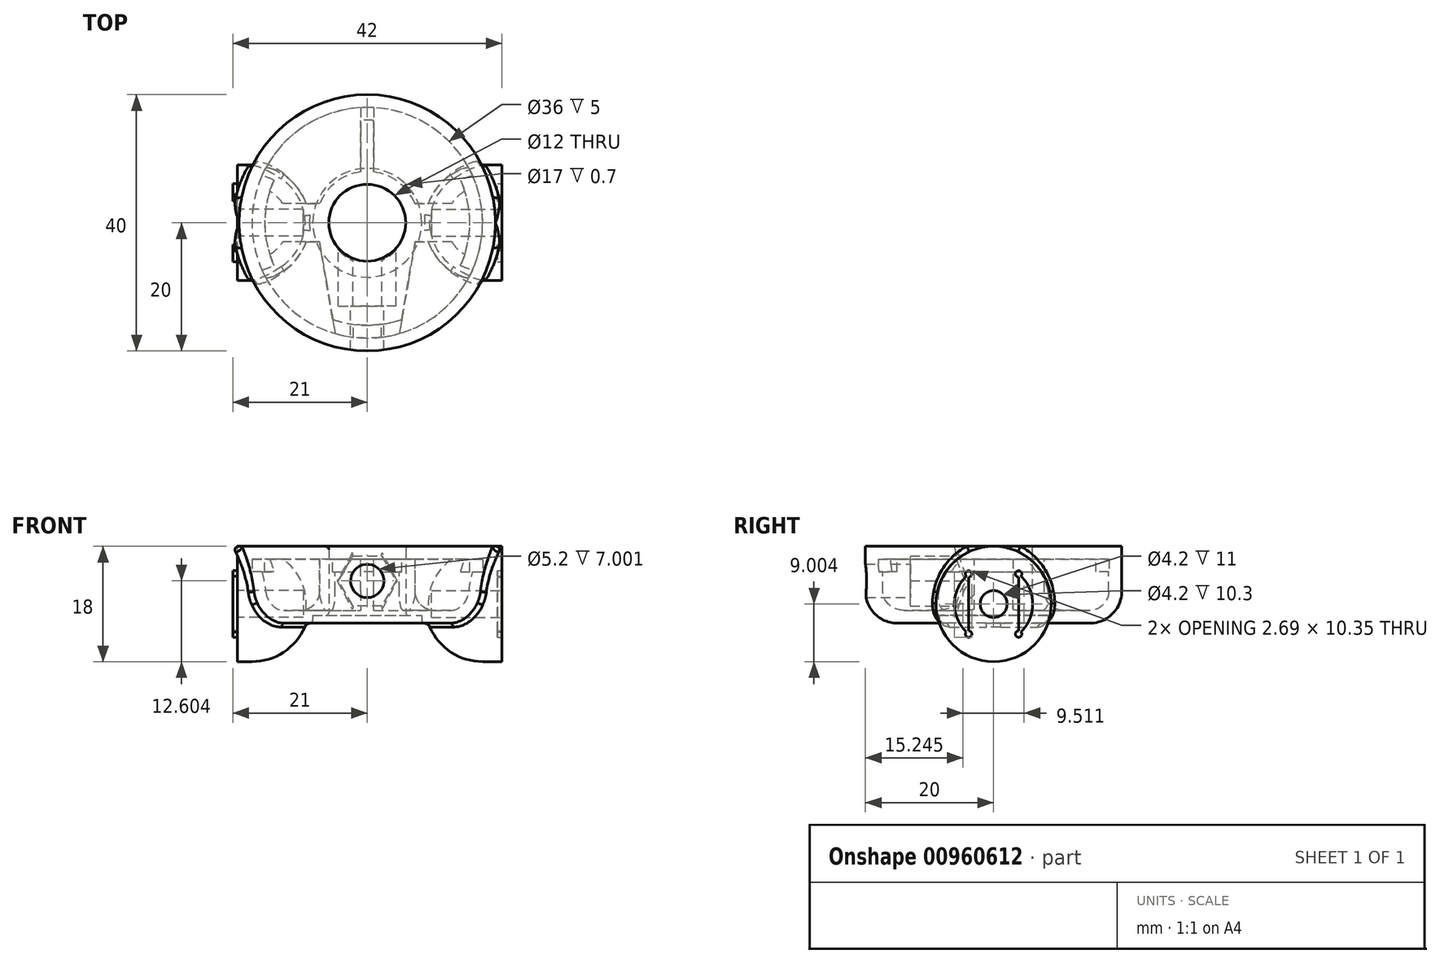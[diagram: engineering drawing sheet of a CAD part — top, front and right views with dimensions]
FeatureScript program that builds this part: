
annotation { "Feature Type Name" : "Feature", "Feature Type Description" : "" }
export const myFeature = defineFeature(function(context is Context, id is Id, definition is map)
    precondition{}
    {
        {
            var Q0;
            Q0=qCreatedBy(makeId("Front.planeOp"),FACE);
            var sketch = newSketch(context, id + "F0", { "sketchPlane" : qUnion([Q0])});
            skLineSegment(sketch, "E0", {"start": v(0, 0) * mm, "end": v(0, 29.29) * mm, "construction": true});
            skLineSegment(sketch, "E1", {"start": v(-6, 15.66) * mm, "end": v(-6, 4.86) * mm});
            skLineSegment(sketch, "E2", {"start": v(-6, 4.86) * mm, "end": v(-8.5, 4.86) * mm});
            skLineSegment(sketch, "E3", {"start": v(-8.5, 4.86) * mm, "end": v(-8.5, 3.66) * mm});
            skLineSegment(sketch, "E4", {"start": v(-8.5, 3.66) * mm, "end": v(-8.5, 3.66) * mm});
            skLineSegment(sketch, "E5", {"start": v(-8.5, 3.66) * mm, "end": v(-15, 3.66) * mm});
            skLineSegment(sketch, "E6", {"start": v(-20, 8.66) * mm, "end": v(-20, 15.66) * mm});
            skLineSegment(sketch, "E7", {"start": v(-20, 15.66) * mm, "end": v(-18, 15.66) * mm});
            skLineSegment(sketch, "E8", {"start": v(-18, 15.66) * mm, "end": v(-18, 15.66) * mm});
            skLineSegment(sketch, "E9", {"start": v(-18, 15.66) * mm, "end": v(-18, 8.66) * mm});
            skLineSegment(sketch, "E10", {"start": v(-15, 5.66) * mm, "end": v(-11, 5.66) * mm});
            skLineSegment(sketch, "E11", {"start": v(-8, 5.66) * mm, "end": v(-8, 5.66) * mm});
            skLineSegment(sketch, "E12", {"start": v(-8, 8.66) * mm, "end": v(-8, 15.66) * mm});
            skLineSegment(sketch, "E13", {"start": v(-6, 15.66) * mm, "end": v(-8, 15.66) * mm});
            skPoint(sketch, "E14.visualSharp", {"position": v(-20, 3.66) * mm});
            skArc(sketch, "E14.filletArc", {"start": v(-20, 8.66) * mm, "mid": v(-18.54, 5.13) * mm, "end": v(-15, 3.66) * mm});
            skPoint(sketch, "E15.visualSharp", {"position": v(-18, 5.66) * mm});
            skArc(sketch, "E15.filletArc", {"start": v(-18, 8.66) * mm, "mid": v(-17.12, 6.54) * mm, "end": v(-15, 5.66) * mm});
            skPoint(sketch, "E16.visualSharp", {"position": v(-8, 5.66) * mm});
            skArc(sketch, "E16.filletArc", {"start": v(-11, 5.66) * mm, "mid": v(-8.88, 6.54) * mm, "end": v(-8, 8.66) * mm});
            skSolve(sketch);
        }
        {
            var Q0;
            Q0=makeQuery(id+"F0.imprint","IMPRINT",FACE,{"disambiguationData":[TD([[makeQuery(id+"F0.imprint","IMPRINT",EDGE,{"derivedFrom":sQuery(id+"F0.wireOp",EDGE,"E1")}),-1.0]])]});
            var Q1;
            Q1=sQuery(id+"F0.wireOp",EDGE,"E0");
            revolve(context, id + "F1", {"surfaceOperationType" : NewSurfaceOperationType.NEW, "entities" : qUnion([Q0]), "axis" : qUnion([Q1]), "revolveType" : RevolveType.FULL});
        }
        {
            var Q0;
            Q0=makeQuery(id+"F1.opRevolve","SWEPT_FACE",FACE,{"disambiguationData":[OSD([sQuery(id+"F0.wireOp",EDGE,"E7")])]});
            cPlane(context, id + "F2", {"entities" : qUnion([Q0]), "cplaneType" : CPlaneType.OFFSET, "offset" : 9 * mm, "oppositeDirection" : true, "width" : 150 * mm, "height" : 150 * mm});
        }
        {
            var Q0;
            Q0=qCreatedBy(id+"F2.planeOp",FACE);
            var sketch = newSketch(context, id + "F3", { "sketchPlane" : qUnion([Q0])});
            skLineSegment(sketch, "E17.bottom", {"start": v(-9, 0) * mm, "end": v(-21, 0) * mm});
            skLineSegment(sketch, "E17.top", {"start": v(-18, -9) * mm, "end": v(-21, -9) * mm});
            skLineSegment(sketch, "E17.left", {"start": v(-9, 0) * mm, "end": v(-9, 0) * mm});
            skLineSegment(sketch, "E17.right", {"start": v(-21, 0) * mm, "end": v(-21, -9) * mm});
            skLineSegment(sketch, "E18.bottom", {"start": v(9, 0) * mm, "end": v(21, 0) * mm});
            skLineSegment(sketch, "E18.top", {"start": v(18, -9) * mm, "end": v(21, -9) * mm});
            skLineSegment(sketch, "E18.left", {"start": v(9, 0) * mm, "end": v(9, 0) * mm});
            skLineSegment(sketch, "E18.right", {"start": v(21, 0) * mm, "end": v(21, -9) * mm});
            skPoint(sketch, "E19.visualSharp", {"position": v(-9, -9) * mm});
            skArc(sketch, "E19.filletArc", {"start": v(-18, -9) * mm, "mid": v(-11.64, -6.36) * mm, "end": v(-9, 0) * mm});
            skPoint(sketch, "E20.visualSharp", {"position": v(9, -9) * mm});
            skArc(sketch, "E20.filletArc", {"start": v(9, 0) * mm, "mid": v(11.64, -6.36) * mm, "end": v(18, -9) * mm});
            skSolve(sketch);
        }
        {
            var Q0;
            Q0=makeQuery(id+"F3.imprint","IMPRINT",FACE,{"disambiguationData":[TD([[makeQuery(id+"F3.imprint","IMPRINT",EDGE,{"derivedFrom":sQuery(id+"F3.wireOp",EDGE,"E17.bottom")}),1.0]])]});
            var Q1;
            Q1=makeQuery(id+"F3.imprint","IMPRINT",FACE,{"disambiguationData":[TD([[makeQuery(id+"F3.imprint","IMPRINT",EDGE,{"derivedFrom":sQuery(id+"F3.wireOp",EDGE,"E18.bottom")}),-1.0]])]});
            var Q2;
            Q2=sQuery(id+"F3.wireOp",EDGE,"E17.bottom");
            revolve(context, id + "F4", {"operationType" : NewBodyOperationType.ADD, "surfaceOperationType" : NewSurfaceOperationType.NEW, "entities" : qUnion([Q0, Q1]), "axis" : qUnion([Q2]), "revolveType" : RevolveType.FULL});
        }
        {
            var Q0;
            Q0=makeQuery(id+"F1.opRevolve","SWEPT_FACE",FACE,{"disambiguationData":[OSD([sQuery(id+"F0.wireOp",EDGE,"E7")])]});
            var sketch = newSketch(context, id + "F5", { "sketchPlane" : qUnion([Q0])});
            skLineSegment(sketch, "E21.bottom", {"start": v(-19.77, 3) * mm, "end": v(19.77, 3) * mm});
            skLineSegment(sketch, "E21.top", {"start": v(-19.77, -3) * mm, "end": v(19.77, -3) * mm});
            skLineSegment(sketch, "E21.left", {"start": v(-19.77, 3) * mm, "end": v(-19.77, -3) * mm});
            skLineSegment(sketch, "E21.right", {"start": v(19.77, 3) * mm, "end": v(19.77, -3) * mm});
            skLineSegment(sketch, "E22", {"start": v(-7, 3) * mm, "end": v(-7, -3) * mm});
            skLineSegment(sketch, "E23", {"start": v(7, 3) * mm, "end": v(7, -3) * mm});
            skSolve(sketch);
        }
        {
            var Q0;
            {var subQ0=sQuery(id+"F5.wireOp",EDGE,"E23");Q0=makeQuery(id+"F5.imprint","IMPRINT",FACE,{"disambiguationData":[TD([[makeQuery(id+"F5.imprint","IMPRINT",EDGE,{"derivedFrom":subQ0}),1.0]])]});}
            var Q1;
            {var subQ0=sQuery(id+"F5.wireOp",EDGE,"E22");Q1=makeQuery(id+"F5.imprint","IMPRINT",FACE,{"disambiguationData":[TD([[makeQuery(id+"F5.imprint","IMPRINT",EDGE,{"derivedFrom":subQ0}),-1.0]])]});}
            extrude(context, id + "F6", {"entities" : qUnion([Q0, Q1]), "operationType" : NewBodyOperationType.ADD, "oppositeDirection" : true, "depth" : 10 * mm, "offsetDistance" : 25 * mm});
        }
        {
            var Q0;
            Q0=makeQuery(id+"F4.opRevolve","SWEPT_FACE",FACE,{"disambiguationData":[OSD([sQuery(id+"F3.wireOp",EDGE,"E18.right")])]});
            var sketch = newSketch(context, id + "F7", { "sketchPlane" : qUnion([Q0])});
            skCircle(sketch, "E24.0", {"center": v(0, 6.66) * mm, "radius": 9 * mm});
            skCircle(sketch, "E25", {"center": v(0, 6.66) * mm, "radius": 2.1 * mm});
            skSolve(sketch);
        }
        {
            var Q0;
            Q0=makeQuery(id+"F7.imprint","IMPRINT",FACE,{"disambiguationData":[TD([[makeQuery(id+"F7.imprint","IMPRINT",EDGE,{"derivedFrom":sQuery(id+"F7.wireOp",EDGE,"E25")}),1.0]])]});
            extrude(context, id + "F8", {"entities" : qUnion([Q0]), "operationType" : NewBodyOperationType.REMOVE, "oppositeDirection" : true, "depth" : 11 * mm, "offsetDistance" : 25 * mm});
        }
        {
            var Q0;
            Q0=makeQuery(id+"F4.opRevolve","SWEPT_FACE",FACE,{"disambiguationData":[OSD([sQuery(id+"F3.wireOp",EDGE,"E17.right")])]});
            var sketch = newSketch(context, id + "F9", { "sketchPlane" : qUnion([Q0])});
            skCircle(sketch, "E26.0", {"center": v(0, 6.66) * mm, "radius": 2.1 * mm});
            skSolve(sketch);
        }
        {
            var Q0;
            Q0=makeQuery(id+"F9.imprint","IMPRINT",FACE,{"disambiguationData":[TD([[makeQuery(id+"F9.imprint","IMPRINT",EDGE,{"derivedFrom":sQuery(id+"F9.wireOp",EDGE,"E26.0")}),1.0]])]});
            extrude(context, id + "F10", {"entities" : qUnion([Q0]), "operationType" : NewBodyOperationType.REMOVE, "oppositeDirection" : true, "depth" : 11 * mm, "offsetDistance" : 25 * mm});
        }
        {
            var Q0;
            {var subQ0=sQuery(id+"F5.wireOp",EDGE,"E21.top");var subQ1=sQuery(id+"F5.wireOp",EDGE,"E21.bottom");var subQ2=sQuery(id+"F0.wireOp",EDGE,"E9");var subQ3=sQuery(id+"F0.wireOp",EDGE,"E7");Q0=makeQuery(id+"F6.boolean.opBoolean","MERGE",FACE,{"derivedFrom":[makeQuery(id+"F1.opRevolve","SWEPT_FACE",FACE,{"disambiguationData":[OSD([subQ3])]}),makeQuery(id+"F1.opRevolve","SWEPT_FACE",FACE,{"disambiguationData":[OSD([sQuery(id+"F0.wireOp",EDGE,"E13")])]}),makeQuery(id+"F6.opExtrude","CAP_FACE",FACE,{"disambiguationData":[OSD([subQ3,subQ2,subQ1,subQ0,sQuery(id+"F5.wireOp",EDGE,"E22")])],"isStart":true}),makeQuery(id+"F6.opExtrude","CAP_FACE",FACE,{"disambiguationData":[OSD([subQ3,subQ2,subQ1,subQ0,sQuery(id+"F5.wireOp",EDGE,"E23")])],"isStart":true})]});}
            var sketch = newSketch(context, id + "F11", { "sketchPlane" : qUnion([Q0])});
            skLineSegment(sketch, "E27", {"start": v(-7.5, -2.78) * mm, "end": v(-5, -17.3) * mm});
            skLineSegment(sketch, "E28", {"start": v(7.5, -2.78) * mm, "end": v(5, -17.3) * mm});
            skSolve(sketch);
        }
        {
            var Q0;
            {var subQ0=sQuery(id+"F11.wireOp",EDGE,"E27");Q0=makeQuery(id+"F11.imprint","IMPRINT",FACE,{"disambiguationData":[TD([[makeQuery(id+"F11.imprint","IMPRINT",EDGE,{"derivedFrom":subQ0}),1.0]])]});}
            extrude(context, id + "F12", {"entities" : qUnion([Q0]), "operationType" : NewBodyOperationType.ADD, "oppositeDirection" : true, "depth" : 10 * mm, "offsetDistance" : 25 * mm});
        }
        {
            var Q0;
            Q0=qCreatedBy(makeId("Front.planeOp"),FACE);
            var sketch = newSketch(context, id + "F13", { "sketchPlane" : qUnion([Q0])});
            skCircle(sketch, "E29", {"center": v(0, 10.26) * mm, "radius": 2.6 * mm});
            skSolve(sketch);
        }
        {
            var Q0;
            Q0 = qSketchRegion(id + "F13", true);
            extrude(context, id + "F14", {"entities" : qUnion([Q0]), "operationType" : NewBodyOperationType.REMOVE, "depth" : 25 * mm, "offsetDistance" : 25 * mm});
        }
        {
            var Q0;
            {var subQ0=sQuery(id+"F0.wireOp",EDGE,"E13");var subQ1=sQuery(id+"F0.wireOp",EDGE,"E9");var subQ2=sQuery(id+"F0.wireOp",EDGE,"E7");var subQ3=sQuery(id+"F5.wireOp",EDGE,"E21.top");var subQ4=sQuery(id+"F5.wireOp",EDGE,"E21.bottom");Q0=makeQuery(id+"F12.boolean.opBoolean","MERGE",FACE,{"derivedFrom":[makeQuery(id+"F6.boolean.opBoolean","MERGE",FACE,{"derivedFrom":[makeQuery(id+"F1.opRevolve","SWEPT_FACE",FACE,{"disambiguationData":[OSD([subQ2])]}),makeQuery(id+"F1.opRevolve","SWEPT_FACE",FACE,{"disambiguationData":[OSD([subQ0])]}),makeQuery(id+"F6.opExtrude","CAP_FACE",FACE,{"disambiguationData":[OSD([subQ2,subQ1,subQ4,subQ3,sQuery(id+"F5.wireOp",EDGE,"E22")])],"isStart":true}),makeQuery(id+"F6.opExtrude","CAP_FACE",FACE,{"disambiguationData":[OSD([subQ2,subQ1,subQ4,subQ3,sQuery(id+"F5.wireOp",EDGE,"E23")])],"isStart":true})]}),makeQuery(id+"F12.opExtrude","CAP_FACE",FACE,{"disambiguationData":[OSD([subQ2,subQ1,sQuery(id+"F0.wireOp",EDGE,"E12"),subQ0,sQuery(id+"F11.wireOp",EDGE,"E27"),sQuery(id+"F11.wireOp",EDGE,"E28")])],"isStart":true})]});}
            var sketch = newSketch(context, id + "F15", { "sketchPlane" : qUnion([Q0])});
            skLineSegment(sketch, "E30.bottom", {"start": v(-1, 18.3) * mm, "end": v(1, 18.3) * mm});
            skLineSegment(sketch, "E30.top", {"start": v(-1, 7.14) * mm, "end": v(1, 7.14) * mm});
            skLineSegment(sketch, "E30.left", {"start": v(-1, 18.3) * mm, "end": v(-1, 7.14) * mm});
            skLineSegment(sketch, "E30.right", {"start": v(1, 18.3) * mm, "end": v(1, 7.14) * mm});
            skSolve(sketch);
        }
        {
            var Q0;
            {var subQ0=sQuery(id+"F15.wireOp",EDGE,"E30.left");var subQ1=sQuery(id+"F5.wireOp",EDGE,"E22");var subQ2=sQuery(id+"F5.wireOp",EDGE,"E21.bottom");var subQ3=sQuery(id+"F0.wireOp",EDGE,"E9");var subQ4=sQuery(id+"F0.wireOp",EDGE,"E7");var subQ5=makeQuery(id+"F1.opRevolve","SWEPT_EDGE",EDGE,{"disambiguationData":[OSD([subQ4,subQ3])]});var subQ6=makeQuery(id+"F6.opExtrude","SWEPT_FACE",FACE,{"disambiguationData":[OSD([subQ2]),TDD([makeQuery(id+"F5.imprint","IMPRINT",EDGE,{"disambiguationData":[TD([[makeQuery(id+"F5.imprint","INTERSECT",VERTEX,{"derivedFrom":[subQ2,subQ1]}),1.0]])],"derivedFrom":subQ2})])]});var subQ15=makeQuery(id+"F6.boolean.opBoolean","SPLIT",EDGE,{"disambiguationData":[TD([subQ6])],"derivedFrom":subQ5});var subQ16=makeQuery(id+"F15.imprint","INTERSECT",VERTEX,{"derivedFrom":[subQ15,subQ0]});Q0=makeQuery(id+"F15.imprint","IMPRINT",FACE,{"disambiguationData":[TD([[makeQuery(id+"F15.imprint","IMPRINT",EDGE,{"disambiguationData":[TD([[subQ16,-1.0]])],"derivedFrom":subQ0}),1.0]])]});}
            extrude(context, id + "F16", {"entities" : qUnion([Q0]), "operationType" : NewBodyOperationType.ADD, "oppositeDirection" : true, "depth" : 10 * mm, "offsetDistance" : 25 * mm});
        }
        {
            var Q0;
            Q0=makeQuery(id+"F1.opRevolve","SWEPT_EDGE",EDGE,{"disambiguationData":[OSD([sQuery(id+"F0.wireOp",EDGE,"E1"),sQuery(id+"F0.wireOp",EDGE,"E2")])]});
            var Q1;
            Q1=makeQuery(id+"F1.opRevolve","SWEPT_EDGE",EDGE,{"disambiguationData":[OSD([sQuery(id+"F0.wireOp",EDGE,"E3"),sQuery(id+"F0.wireOp",EDGE,"E5")])]});
            var Q2;
            Q2=makeQuery(id+"F1.opRevolve","SWEPT_EDGE",EDGE,{"disambiguationData":[OSD([sQuery(id+"F0.wireOp",EDGE,"E1"),sQuery(id+"F0.wireOp",EDGE,"E13")])]});
            var Q3;
            Q3=makeQuery(id+"F28.boolean.opBoolean","INTERSECT",EDGE,{"derivedFrom":[makeQuery(id+"F1.opRevolve","SWEPT_FACE",FACE,{"disambiguationData":[OSD([sQuery(id+"F0.wireOp",EDGE,"E1")])]}),makeQuery(id+"F28.opExtrude","SWEPT_FACE",FACE,{"disambiguationData":[OSD([sQuery(id+"F27.wireOp",EDGE,"E51.5")])]})]});
            var Q4;
            Q4=makeQuery(id+"F28.boolean.opBoolean","INTERSECT",EDGE,{"derivedFrom":[makeQuery(id+"F1.opRevolve","SWEPT_FACE",FACE,{"disambiguationData":[OSD([sQuery(id+"F0.wireOp",EDGE,"E1")])]}),makeQuery(id+"F28.opExtrude","SWEPT_FACE",FACE,{"disambiguationData":[OSD([sQuery(id+"F27.wireOp",EDGE,"E51.4")])]})]});
            var Q5;
            Q5=makeQuery(id+"F28.boolean.opBoolean","INTERSECT",EDGE,{"derivedFrom":[makeQuery(id+"F1.opRevolve","SWEPT_FACE",FACE,{"disambiguationData":[OSD([sQuery(id+"F0.wireOp",EDGE,"E1")])]}),makeQuery(id+"F28.opExtrude","SWEPT_FACE",FACE,{"disambiguationData":[OSD([sQuery(id+"F27.wireOp",EDGE,"E51.3")])]})]});
            var Q6;
            Q6=makeQuery(id+"F28.boolean.opBoolean","INTERSECT",EDGE,{"derivedFrom":[makeQuery(id+"F1.opRevolve","SWEPT_FACE",FACE,{"disambiguationData":[OSD([sQuery(id+"F0.wireOp",EDGE,"E1")])]}),makeQuery(id+"F28.opExtrude","SWEPT_FACE",FACE,{"disambiguationData":[OSD([sQuery(id+"F27.wireOp",EDGE,"E51.2")])]})]});
            var Q7;
            Q7=makeQuery(id+"F28.boolean.opBoolean","INTERSECT",EDGE,{"derivedFrom":[makeQuery(id+"F1.opRevolve","SWEPT_FACE",FACE,{"disambiguationData":[OSD([sQuery(id+"F0.wireOp",EDGE,"E1")])]}),makeQuery(id+"F28.opExtrude","SWEPT_FACE",FACE,{"disambiguationData":[OSD([sQuery(id+"F27.wireOp",EDGE,"E51.1")])]})]});
            var Q8;
            Q8=makeQuery(id+"F28.boolean.opBoolean","INTERSECT",EDGE,{"derivedFrom":[makeQuery(id+"F1.opRevolve","SWEPT_FACE",FACE,{"disambiguationData":[OSD([sQuery(id+"F0.wireOp",EDGE,"E1")])]}),makeQuery(id+"F28.opExtrude","SWEPT_FACE",FACE,{"disambiguationData":[OSD([sQuery(id+"F27.wireOp",EDGE,"E51.0")])]})]});
            fillet(context, id + "F17", {"entities" : qUnion([Q0, Q1, Q2, Q3, Q4, Q5, Q6, Q7, Q8]), "radius" : 0.5 * mm, "tangentPropagation" : true, "allowEdgeOverflow" : false});
        }
        {
            var Q0;
            Q0=qCreatedBy(makeId("Right.planeOp"),FACE);
            var sketch = newSketch(context, id + "F18", { "sketchPlane" : qUnion([Q0])});
            skLineSegment(sketch, "E31.bottom", {"start": v(18, 18.33) * mm, "end": v(16, 18.33) * mm});
            skLineSegment(sketch, "E31.top", {"start": v(18, 11.66) * mm, "end": v(16, 11.66) * mm});
            skLineSegment(sketch, "E31.left", {"start": v(18, 18.33) * mm, "end": v(18, 11.66) * mm});
            skLineSegment(sketch, "E31.right", {"start": v(16, 18.33) * mm, "end": v(16, 11.66) * mm});
            skLineSegment(sketch, "E32", {"start": v(0, 0) * mm, "end": v(0, 18.33) * mm, "construction": true});
            skSolve(sketch);
        }
        {
            var Q0;
            Q0=makeQuery(id+"F18.imprint","IMPRINT",FACE,{"disambiguationData":[TD([[makeQuery(id+"F18.imprint","IMPRINT",EDGE,{"derivedFrom":sQuery(id+"F18.wireOp",EDGE,"E31.bottom")}),1.0]])]});
            var Q1;
            Q1=sQuery(id+"F18.wireOp",EDGE,"E32");
            revolve(context, id + "F19", {"operationType" : NewBodyOperationType.REMOVE, "surfaceOperationType" : NewSurfaceOperationType.NEW, "entities" : qUnion([Q0]), "axis" : qUnion([Q1]), "revolveType" : RevolveType.FULL, "oppositeDirection" : true});
        }
        {
            var Q0;
            Q0=makeQuery(id+"F4.boolean.opBoolean","INTERSECT",EDGE,{"derivedFrom":[makeQuery(id+"F1.opRevolve","SWEPT_FACE",FACE,{"disambiguationData":[OSD([sQuery(id+"F0.wireOp",EDGE,"E5")])]}),makeQuery(id+"F4.opRevolve","SWEPT_FACE",FACE,{"disambiguationData":[OSD([sQuery(id+"F3.wireOp",EDGE,"E20.filletArc")])]})]});
            var Q1;
            Q1=makeQuery(id+"F4.boolean.opBoolean","INTERSECT",EDGE,{"derivedFrom":[makeQuery(id+"F1.opRevolve","SWEPT_FACE",FACE,{"disambiguationData":[OSD([sQuery(id+"F0.wireOp",EDGE,"E5")])]}),makeQuery(id+"F4.opRevolve","SWEPT_FACE",FACE,{"disambiguationData":[OSD([sQuery(id+"F3.wireOp",EDGE,"E19.filletArc")])]})]});
            fillet(context, id + "F20", {"entities" : qUnion([Q0, Q1]), "radius" : 1 * mm, "tangentPropagation" : true, "allowEdgeOverflow" : false});
        }
        {
            var Q0;
            {var subQ2=sQuery(id+"F0.wireOp",EDGE,"E6");var subQ3=makeQuery(id+"F1.opRevolve","SWEPT_FACE",FACE,{"disambiguationData":[OSD([subQ2])]});var subQ6=sQuery(id+"F0.wireOp",EDGE,"E9");var subQ11=sQuery(id+"F0.wireOp",EDGE,"E13");var subQ12=sQuery(id+"F0.wireOp",EDGE,"E12");var subQ13=sQuery(id+"F0.wireOp",EDGE,"E7");var subQ14=sQuery(id+"F5.wireOp",EDGE,"E21.top");var subQ15=sQuery(id+"F5.wireOp",EDGE,"E21.bottom");Q0=makeQuery(id+"F19.boolean.opBoolean","SPLIT",FACE,{"disambiguationData":[TD([subQ3])],"derivedFrom":makeQuery(id+"F16.boolean.opBoolean","MERGE",FACE,{"derivedFrom":[makeQuery(id+"F12.boolean.opBoolean","MERGE",FACE,{"derivedFrom":[makeQuery(id+"F6.boolean.opBoolean","MERGE",FACE,{"derivedFrom":[makeQuery(id+"F1.opRevolve","SWEPT_FACE",FACE,{"disambiguationData":[OSD([subQ13])]}),makeQuery(id+"F1.opRevolve","SWEPT_FACE",FACE,{"disambiguationData":[OSD([subQ11])]}),makeQuery(id+"F6.opExtrude","CAP_FACE",FACE,{"disambiguationData":[OSD([subQ13,subQ6,subQ15,subQ14,sQuery(id+"F5.wireOp",EDGE,"E22")])],"isStart":true}),makeQuery(id+"F6.opExtrude","CAP_FACE",FACE,{"disambiguationData":[OSD([subQ13,subQ6,subQ15,subQ14,sQuery(id+"F5.wireOp",EDGE,"E23")])],"isStart":true})]}),makeQuery(id+"F12.opExtrude","CAP_FACE",FACE,{"disambiguationData":[OSD([subQ13,subQ6,subQ12,subQ11,subQ14,sQuery(id+"F11.wireOp",EDGE,"E27"),sQuery(id+"F11.wireOp",EDGE,"E28")])],"isStart":true})]}),makeQuery(id+"F16.opExtrude","CAP_FACE",FACE,{"disambiguationData":[OSD([subQ13,subQ6,subQ12,subQ11,sQuery(id+"F15.wireOp",EDGE,"E30.left"),sQuery(id+"F15.wireOp",EDGE,"E30.right")])],"isStart":true})]})});}
            var sketch = newSketch(context, id + "F21", { "sketchPlane" : qUnion([Q0])});
            skCircle(sketch, "E33", {"center": v(0, 0) * mm, "radius": 20 * mm});
            skCircle(sketch, "E34", {"center": v(0, 0) * mm, "radius": 7 * mm});
            skSolve(sketch);
        }
        {
            var Q0;
            {var subQ0=sQuery(id+"F21.wireOp",EDGE,"E33");var subQ5=makeQuery(id+"F21.imprint","IMPRINT",VERTEX,{"disambiguationData":[OD(0.0)],"derivedFrom":subQ0});Q0=makeQuery(id+"F21.imprint","IMPRINT",FACE,{"disambiguationData":[TD([[makeQuery(id+"F21.imprint","IMPRINT",EDGE,{"disambiguationData":[TD([[subQ5,-1.0]])],"derivedFrom":subQ0}),-1.0]])]});}
            var Q1;
            Q1=makeQuery(id+"F21.imprint","IMPRINT",FACE,{"disambiguationData":[TD([[makeQuery(id+"F21.imprint","IMPRINT",EDGE,{"derivedFrom":sQuery(id+"F21.wireOp",EDGE,"E34")}),-1.0]])]});
            extrude(context, id + "F22", {"entities" : qUnion([Q0, Q1]), "operationType" : NewBodyOperationType.ADD, "oppositeDirection" : true, "depth" : 2 * mm, "offsetDistance" : 25 * mm});
        }
        {
            var Q0;
            Q0=makeQuery(id+"F4.opRevolve","SWEPT_FACE",FACE,{"disambiguationData":[OSD([sQuery(id+"F3.wireOp",EDGE,"E18.right")])]});
            var sketch = newSketch(context, id + "F23", { "sketchPlane" : qUnion([Q0])});
            skCircle(sketch, "E35.0", {"center": v(0, 6.66) * mm, "radius": 2.1 * mm});
            skArc(sketch, "E36", {"start": v(-4.27, 11.02) * mm, "mid": v(-6.1, 6.66) * mm, "end": v(-4.27, 2.3) * mm, "construction": true});
            skLineSegment(sketch, "E37", {"start": v(-3.9, 10.85) * mm, "end": v(-3.9, 2.47) * mm});
            skLineSegment(sketch, "E38", {"start": v(3.9, 10.85) * mm, "end": v(3.9, 2.47) * mm});
            skArc(sketch, "E39", {"start": v(-3.9, 10.85) * mm, "mid": v(-3.7, 11.81) * mm, "end": v(-4.27, 11.02) * mm});
            skArc(sketch, "E40", {"start": v(4.27, 11.02) * mm, "mid": v(3.7, 11.81) * mm, "end": v(3.9, 10.85) * mm});
            skArc(sketch, "E41", {"start": v(3.9, 2.47) * mm, "mid": v(3.7, 1.52) * mm, "end": v(4.27, 2.3) * mm});
            skArc(sketch, "E42", {"start": v(-4.27, 2.3) * mm, "mid": v(-3.7, 1.52) * mm, "end": v(-3.9, 2.47) * mm});
            skArc(sketch, "E43", {"start": v(-4.27, 11.02) * mm, "mid": v(-6.1, 6.66) * mm, "end": v(-4.27, 2.3) * mm});
            skArc(sketch, "E44", {"start": v(4.27, 11.02) * mm, "mid": v(6.1, 6.66) * mm, "end": v(4.27, 2.3) * mm});
            skArc(sketch, "E45.trimOffspring", {"start": v(3.5, 11.66) * mm, "mid": v(0, 12.76) * mm, "end": v(-3.5, 11.66) * mm, "construction": true});
            skArc(sketch, "E46.trimOffspring", {"start": v(4.27, 2.3) * mm, "mid": v(6.1, 6.66) * mm, "end": v(4.27, 11.02) * mm, "construction": true});
            skArc(sketch, "E47.trimOffspring", {"start": v(-3.9, 1.97) * mm, "mid": v(-0.25, 0.57) * mm, "end": v(3.5, 1.67) * mm, "construction": true});
            skSolve(sketch);
        }
        {
            var Q0;
            Q0=makeQuery(id+"F23.imprint","IMPRINT",FACE,{"disambiguationData":[TD([[makeQuery(id+"F23.imprint","IMPRINT",EDGE,{"derivedFrom":sQuery(id+"F23.wireOp",EDGE,"E37")}),-1.0]])]});
            var Q1;
            Q1=makeQuery(id+"F23.imprint","IMPRINT",FACE,{"disambiguationData":[TD([[makeQuery(id+"F23.imprint","IMPRINT",EDGE,{"derivedFrom":sQuery(id+"F23.wireOp",EDGE,"E38")}),1.0]])]});
            extrude(context, id + "F24", {"entities" : qUnion([Q0, Q1]), "operationType" : NewBodyOperationType.REMOVE, "oppositeDirection" : true, "depth" : .7 * mm, "offsetDistance" : 25 * mm});
        }
        {
            var Q0;
            Q0=makeQuery(id+"F4.opRevolve","SWEPT_FACE",FACE,{"disambiguationData":[OSD([sQuery(id+"F3.wireOp",EDGE,"E17.right")])]});
            var sketch = newSketch(context, id + "F25", { "sketchPlane" : qUnion([Q0])});
            skArc(sketch, "E48.0.0", {"start": v(-4.27, 2.3) * mm, "mid": v(-6.1, 6.66) * mm, "end": v(-4.27, 11.02) * mm});
            skArc(sketch, "E48.0.1", {"start": v(-4.27, 11.02) * mm, "mid": v(-3.7, 11.81) * mm, "end": v(-3.9, 10.85) * mm});
            skLineSegment(sketch, "E48.0.2", {"start": v(-3.9, 10.85) * mm, "end": v(-3.9, 2.47) * mm});
            skArc(sketch, "E48.0.3", {"start": v(-3.9, 2.47) * mm, "mid": v(-3.7, 1.52) * mm, "end": v(-4.27, 2.3) * mm});
            skArc(sketch, "E49.0.0", {"start": v(3.9, 10.85) * mm, "mid": v(3.7, 11.81) * mm, "end": v(4.27, 11.02) * mm});
            skArc(sketch, "E49.0.1", {"start": v(4.27, 11.02) * mm, "mid": v(6.1, 6.66) * mm, "end": v(4.27, 2.3) * mm});
            skArc(sketch, "E49.0.2", {"start": v(4.27, 2.3) * mm, "mid": v(3.7, 1.52) * mm, "end": v(3.9, 2.47) * mm});
            skLineSegment(sketch, "E49.0.3", {"start": v(3.9, 2.47) * mm, "end": v(3.9, 10.85) * mm});
            skSolve(sketch);
        }
        {
            var Q0;
            Q0=makeQuery(id+"F25.imprint","IMPRINT",FACE,{"disambiguationData":[TD([[makeQuery(id+"F25.imprint","IMPRINT",EDGE,{"derivedFrom":sQuery(id+"F25.wireOp",EDGE,"E49.0.0")}),-1.0]])]});
            var Q1;
            Q1=makeQuery(id+"F25.imprint","IMPRINT",FACE,{"disambiguationData":[TD([[makeQuery(id+"F25.imprint","IMPRINT",EDGE,{"derivedFrom":sQuery(id+"F25.wireOp",EDGE,"E48.0.0")}),-1.0]])]});
            extrude(context, id + "F26", {"entities" : qUnion([Q0, Q1]), "operationType" : NewBodyOperationType.REMOVE, "oppositeDirection" : true, "depth" : .7 * mm, "offsetDistance" : 25 * mm});
        }
        {
            var Q0;
            Q0=qCreatedBy(makeId("Front.planeOp"),FACE);
            var sketch = newSketch(context, id + "F27", { "sketchPlane" : qUnion([Q0])});
            skArc(sketch, "E50.0", {"start": v(-2.05, 8.66) * mm, "mid": v(0, 12.86) * mm, "end": v(2.05, 8.66) * mm});
            skCircle(sketch, "E51.cCircle", {"center": v(0, 10.26) * mm, "radius": 3.9 * mm, "construction": true});
            skLineSegment(sketch, "E51.0", {"start": v(-2.25, 14.16) * mm, "end": v(2.25, 14.16) * mm});
            skLineSegment(sketch, "E51.1", {"start": v(2.25, 14.16) * mm, "end": v(4.5, 10.26) * mm});
            skLineSegment(sketch, "E51.2", {"start": v(4.5, 10.26) * mm, "end": v(2.25, 6.36) * mm});
            skLineSegment(sketch, "E51.3", {"start": v(2.25, 6.36) * mm, "end": v(-2.25, 6.36) * mm});
            skLineSegment(sketch, "E51.4", {"start": v(-2.25, 6.36) * mm, "end": v(-4.5, 10.26) * mm});
            skLineSegment(sketch, "E51.5", {"start": v(-4.5, 10.26) * mm, "end": v(-2.25, 14.16) * mm});
            skPoint(sketch, "E51.0.midPoint", {"position": v(0, 14.16) * mm});
            skSolve(sketch);
        }
        {
            var Q0;
            Q0=makeQuery(id+"F27.imprint","IMPRINT",FACE,{"disambiguationData":[TD([[makeQuery(id+"F27.imprint","IMPRINT",EDGE,{"derivedFrom":sQuery(id+"F27.wireOp",EDGE,"E51.0")}),-1.0]])]});
            extrude(context, id + "F28", {"entities" : qUnion([Q0]), "operationType" : NewBodyOperationType.REMOVE, "depth" : 13 * mm, "offsetDistance" : 25 * mm});
        }
        {
            var Q0;
            Q0=makeQuery(id+"F28.boolean.opBoolean","INTERSECT",EDGE,{"derivedFrom":[makeQuery(id+"F1.opRevolve","SWEPT_FACE",FACE,{"disambiguationData":[OSD([sQuery(id+"F0.wireOp",EDGE,"E1")])]}),makeQuery(id+"F28.opExtrude","SWEPT_FACE",FACE,{"disambiguationData":[OSD([sQuery(id+"F27.wireOp",EDGE,"E51.2")])]})]});
            var Q1;
            Q1=makeQuery(id+"F28.boolean.opBoolean","INTERSECT",EDGE,{"derivedFrom":[makeQuery(id+"F1.opRevolve","SWEPT_FACE",FACE,{"disambiguationData":[OSD([sQuery(id+"F0.wireOp",EDGE,"E1")])]}),makeQuery(id+"F28.opExtrude","SWEPT_FACE",FACE,{"disambiguationData":[OSD([sQuery(id+"F27.wireOp",EDGE,"E51.1")])]})]});
            var Q2;
            Q2=makeQuery(id+"F28.boolean.opBoolean","INTERSECT",EDGE,{"derivedFrom":[makeQuery(id+"F1.opRevolve","SWEPT_FACE",FACE,{"disambiguationData":[OSD([sQuery(id+"F0.wireOp",EDGE,"E1")])]}),makeQuery(id+"F28.opExtrude","SWEPT_FACE",FACE,{"disambiguationData":[OSD([sQuery(id+"F27.wireOp",EDGE,"E51.0")])]})]});
            var Q3;
            Q3=makeQuery(id+"F28.boolean.opBoolean","INTERSECT",EDGE,{"derivedFrom":[makeQuery(id+"F1.opRevolve","SWEPT_FACE",FACE,{"disambiguationData":[OSD([sQuery(id+"F0.wireOp",EDGE,"E1")])]}),makeQuery(id+"F28.opExtrude","SWEPT_FACE",FACE,{"disambiguationData":[OSD([sQuery(id+"F27.wireOp",EDGE,"E51.5")])]})]});
            var Q4;
            Q4=makeQuery(id+"F28.boolean.opBoolean","INTERSECT",EDGE,{"derivedFrom":[makeQuery(id+"F1.opRevolve","SWEPT_FACE",FACE,{"disambiguationData":[OSD([sQuery(id+"F0.wireOp",EDGE,"E1")])]}),makeQuery(id+"F28.opExtrude","SWEPT_FACE",FACE,{"disambiguationData":[OSD([sQuery(id+"F27.wireOp",EDGE,"E51.4")])]})]});
            var Q5;
            Q5=makeQuery(id+"F28.boolean.opBoolean","INTERSECT",EDGE,{"derivedFrom":[makeQuery(id+"F1.opRevolve","SWEPT_FACE",FACE,{"disambiguationData":[OSD([sQuery(id+"F0.wireOp",EDGE,"E1")])]}),makeQuery(id+"F28.opExtrude","SWEPT_FACE",FACE,{"disambiguationData":[OSD([sQuery(id+"F27.wireOp",EDGE,"E51.3")])]})]});
            fillet(context, id + "F29", {"entities" : qUnion([Q0, Q1, Q2, Q3, Q4, Q5]), "radius" : .5 * mm, "tangentPropagation" : true, "allowEdgeOverflow" : false});
        }
    });
